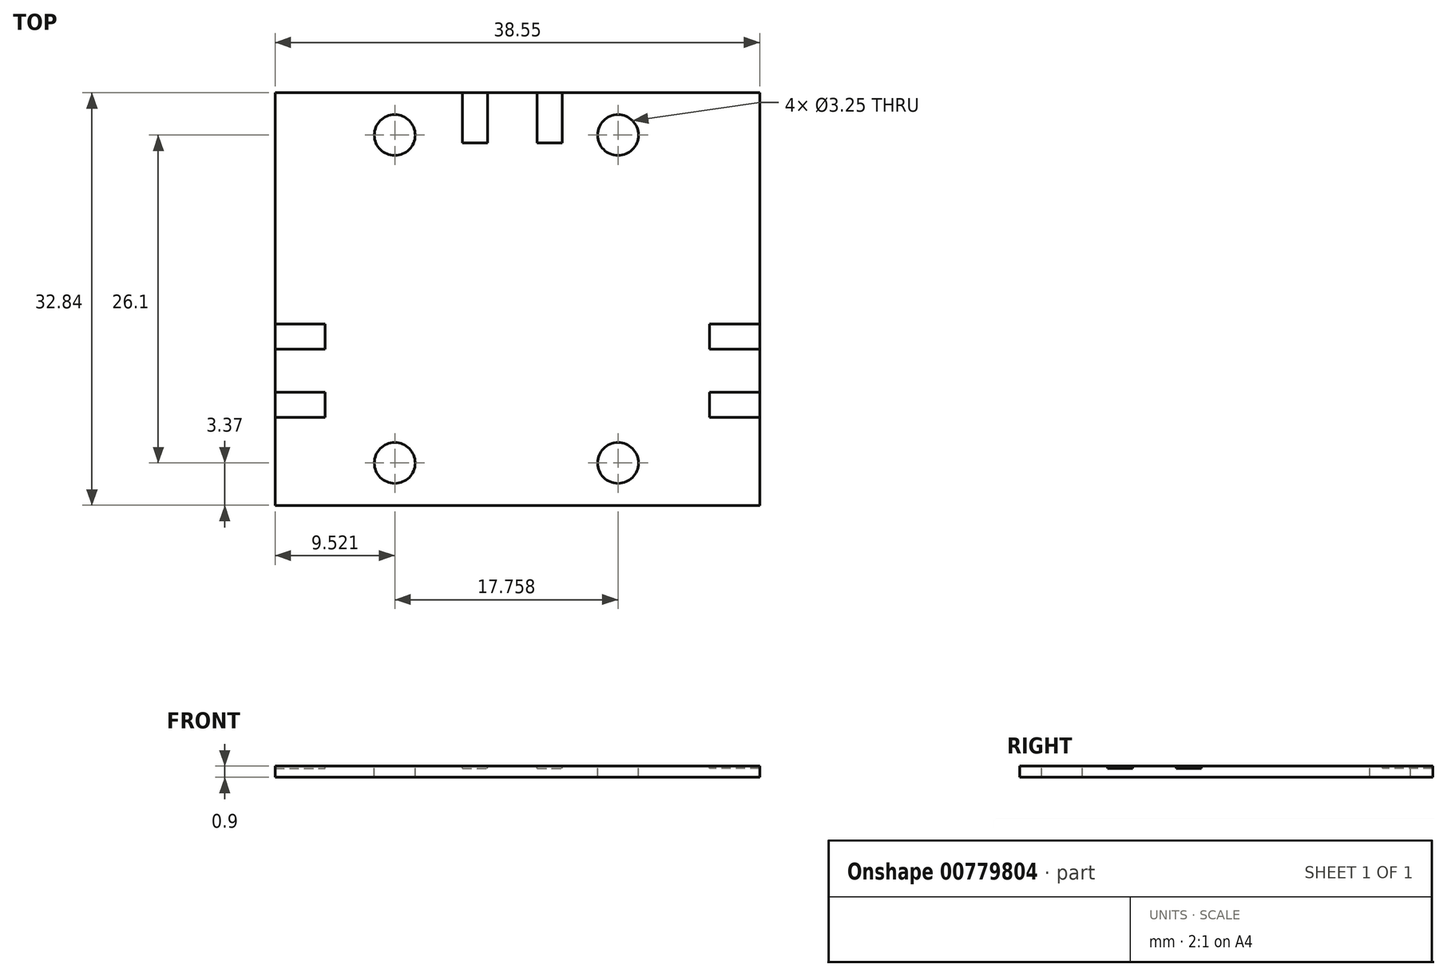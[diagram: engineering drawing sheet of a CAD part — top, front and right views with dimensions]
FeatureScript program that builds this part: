
annotation { "Feature Type Name" : "Feature", "Feature Type Description" : "" }
export const myFeature = defineFeature(function(context is Context, id is Id, definition is map)
    precondition{}
    {
        {
            var Q0;
            Q0=qCreatedBy(makeId("Top.planeOp"),FACE);
            var sketch = newSketch(context, id + "F0", { "sketchPlane" : qUnion([Q0])});
            skLineSegment(sketch, "E0.bottom", {"start": v(-18.4, 16.43) * mm, "end": v(20.15, 16.43) * mm});
            skLineSegment(sketch, "E0.top", {"start": v(-18.4, -16.43) * mm, "end": v(20.15, -16.43) * mm});
            skLineSegment(sketch, "E0.left", {"start": v(-18.4, 16.43) * mm, "end": v(-18.4, -16.43) * mm});
            skLineSegment(sketch, "E0.right", {"start": v(20.15, 16.43) * mm, "end": v(20.15, -16.43) * mm});
            skPoint(sketch, "E0.middle", {"position": v(0.87, 0) * mm});
            skSolve(sketch);
        }
        {
            var Q0;
            Q0=makeQuery(id+"F0.imprint","IMPRINT",FACE,{"disambiguationData":[TD([[makeQuery(id+"F0.imprint","IMPRINT",EDGE,{"derivedFrom":sQuery(id+"F0.wireOp",EDGE,"E0.bottom")}),-1.0]])]});
            extrude(context, id + "F1", {"entities" : qUnion([Q0]), "depth" : 0.9 * mm, "offsetDistance" : 25 * mm});
        }
        {
            var Q0;
            Q0=makeQuery(id+"F1.opExtrude","CAP_FACE",FACE,{"disambiguationData":[OSD([sQuery(id+"F0.wireOp",EDGE,"E0.bottom"),sQuery(id+"F0.wireOp",EDGE,"E0.top"),sQuery(id+"F0.wireOp",EDGE,"E0.left"),sQuery(id+"F0.wireOp",EDGE,"E0.right")])],"isStart":false});
            var sketch = newSketch(context, id + "F2", { "sketchPlane" : qUnion([Q0])});
            skCircle(sketch, "E1", {"center": v(-8.88, -13.05) * mm, "radius": 1.62 * mm});
            skCircle(sketch, "E2.MirrorC", {"center": v(-8.88, 13.05) * mm, "radius": 1.62 * mm});
            skCircle(sketch, "E3.MirrorC", {"center": v(8.88, 13.05) * mm, "radius": 1.62 * mm});
            skCircle(sketch, "E4.MirrorC", {"center": v(8.88, -13.05) * mm, "radius": 1.62 * mm});
            skSolve(sketch);
        }
        {
            var Q0;
            Q0=sQuery(id+"F2.wireOp",VERTEX,"E2.MirrorC.center");
            var Q1;
            Q1=sQuery(id+"F2.wireOp",VERTEX,"E3.MirrorC.center");
            var Q2;
            Q2=sQuery(id+"F2.wireOp",VERTEX,"E4.MirrorC.center");
            var Q3;
            Q3=sQuery(id+"F2.wireOp",VERTEX,"E1.center");
            var Q4;
            Q4=makeQuery(id+"F1.opExtrude","SWEPT_BODY",BODY,{"disambiguationData":[OSD([sQuery(id+"F0.wireOp",EDGE,"E0.bottom"),sQuery(id+"F0.wireOp",EDGE,"E0.top"),sQuery(id+"F0.wireOp",EDGE,"E0.left"),sQuery(id+"F0.wireOp",EDGE,"E0.right")])]});
            hole(context, id + "F3", {"style" : HoleStyle.SIMPLE, "endStyle" : HoleEndStyle.THROUGH, "holeDiameter" : 3.25 * mm, "majorDiameter" : 5 * mm, "isTappedThrough" : true, "tappedDepth" : 12 * mm, "tapClearance" : 3, "locations" : qUnion([Q0, Q1, Q2, Q3]), "scope" : qUnion([Q4])});
        }
        {
            var Q0;
            Q0=makeQuery(id+"F1.opExtrude","CAP_FACE",FACE,{"disambiguationData":[OSD([sQuery(id+"F0.wireOp",EDGE,"E0.bottom"),sQuery(id+"F0.wireOp",EDGE,"E0.top"),sQuery(id+"F0.wireOp",EDGE,"E0.left"),sQuery(id+"F0.wireOp",EDGE,"E0.right")])],"isStart":false});
            var sketch = newSketch(context, id + "F4", { "sketchPlane" : qUnion([Q0])});
            skLineSegment(sketch, "E5.bottom", {"start": v(20.15, -7.43) * mm, "end": v(16.15, -7.43) * mm});
            skLineSegment(sketch, "E5.top", {"start": v(20.15, -9.43) * mm, "end": v(16.15, -9.43) * mm});
            skLineSegment(sketch, "E5.left", {"start": v(20.15, -7.43) * mm, "end": v(20.15, -9.43) * mm});
            skLineSegment(sketch, "E5.right", {"start": v(16.15, -7.43) * mm, "end": v(16.15, -9.43) * mm});
            skLineSegment(sketch, "E6.bottom", {"start": v(20.15, -1.98) * mm, "end": v(16.15, -1.98) * mm});
            skLineSegment(sketch, "E6.top", {"start": v(20.15, -3.98) * mm, "end": v(16.15, -3.98) * mm});
            skLineSegment(sketch, "E6.left", {"start": v(20.15, -1.98) * mm, "end": v(20.15, -3.98) * mm});
            skLineSegment(sketch, "E6.right", {"start": v(16.15, -1.98) * mm, "end": v(16.15, -3.98) * mm});
            skLineSegment(sketch, "E7.bottom", {"start": v(-18.4, -9.43) * mm, "end": v(-14.4, -9.43) * mm});
            skLineSegment(sketch, "E7.top", {"start": v(-18.4, -7.43) * mm, "end": v(-14.4, -7.43) * mm});
            skLineSegment(sketch, "E7.left", {"start": v(-18.4, -9.43) * mm, "end": v(-18.4, -7.43) * mm});
            skLineSegment(sketch, "E7.right", {"start": v(-14.4, -9.43) * mm, "end": v(-14.4, -7.43) * mm});
            skLineSegment(sketch, "E8.bottom", {"start": v(-18.4, -1.98) * mm, "end": v(-14.4, -1.98) * mm});
            skLineSegment(sketch, "E8.top", {"start": v(-18.4, -3.98) * mm, "end": v(-14.4, -3.98) * mm});
            skLineSegment(sketch, "E8.left", {"start": v(-18.4, -1.98) * mm, "end": v(-18.4, -3.98) * mm});
            skLineSegment(sketch, "E8.right", {"start": v(-14.4, -1.98) * mm, "end": v(-14.4, -3.98) * mm});
            skLineSegment(sketch, "E9.bottom", {"start": v(4.45, 16.43) * mm, "end": v(2.45, 16.43) * mm});
            skLineSegment(sketch, "E9.top", {"start": v(4.45, 12.43) * mm, "end": v(2.45, 12.43) * mm});
            skLineSegment(sketch, "E9.left", {"start": v(4.45, 16.43) * mm, "end": v(4.45, 12.43) * mm});
            skLineSegment(sketch, "E9.right", {"start": v(2.45, 16.43) * mm, "end": v(2.45, 12.43) * mm});
            skLineSegment(sketch, "E10.bottom", {"start": v(-3.5, 16.43) * mm, "end": v(-1.5, 16.43) * mm});
            skLineSegment(sketch, "E10.top", {"start": v(-3.5, 12.43) * mm, "end": v(-1.5, 12.43) * mm});
            skLineSegment(sketch, "E10.left", {"start": v(-3.5, 16.43) * mm, "end": v(-3.5, 12.43) * mm});
            skLineSegment(sketch, "E10.right", {"start": v(-1.5, 16.43) * mm, "end": v(-1.5, 12.43) * mm});
            skSolve(sketch);
        }
        {
            var Q0;
            Q0=makeQuery(id+"F4.imprint","IMPRINT",FACE,{"disambiguationData":[TD([[makeQuery(id+"F4.imprint","IMPRINT",EDGE,{"derivedFrom":sQuery(id+"F4.wireOp",EDGE,"E10.bottom")}),-1.0]])]});
            var Q1;
            Q1=makeQuery(id+"F4.imprint","IMPRINT",FACE,{"disambiguationData":[TD([[makeQuery(id+"F4.imprint","IMPRINT",EDGE,{"derivedFrom":sQuery(id+"F4.wireOp",EDGE,"E9.bottom")}),-1.0]])]});
            var Q2;
            Q2=makeQuery(id+"F4.imprint","IMPRINT",FACE,{"disambiguationData":[TD([[makeQuery(id+"F4.imprint","IMPRINT",EDGE,{"derivedFrom":sQuery(id+"F4.wireOp",EDGE,"E6.bottom")}),1.0]])]});
            var Q3;
            Q3=makeQuery(id+"F4.imprint","IMPRINT",FACE,{"disambiguationData":[TD([[makeQuery(id+"F4.imprint","IMPRINT",EDGE,{"derivedFrom":sQuery(id+"F4.wireOp",EDGE,"E5.bottom")}),1.0]])]});
            var Q4;
            Q4=makeQuery(id+"F4.imprint","IMPRINT",FACE,{"disambiguationData":[TD([[makeQuery(id+"F4.imprint","IMPRINT",EDGE,{"derivedFrom":sQuery(id+"F4.wireOp",EDGE,"E7.bottom")}),1.0]])]});
            var Q5;
            Q5=makeQuery(id+"F4.imprint","IMPRINT",FACE,{"disambiguationData":[TD([[makeQuery(id+"F4.imprint","IMPRINT",EDGE,{"derivedFrom":sQuery(id+"F4.wireOp",EDGE,"E8.bottom")}),-1.0]])]});
            extrude(context, id + "F5", {"entities" : qUnion([Q0, Q1, Q2, Q3, Q4, Q5]), "operationType" : NewBodyOperationType.REMOVE, "oppositeDirection" : true, "depth" : 0.2 * mm, "offsetDistance" : 25 * mm});
        }
    });
